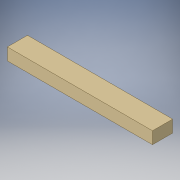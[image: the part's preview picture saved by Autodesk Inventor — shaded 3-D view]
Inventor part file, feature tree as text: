
AUTODESK INVENTOR PART (.ipt)
format: ipt  version: 2016 (Build 200138000, 138)  size: 89,088 bytes
history: native  units: in
note: dims shown in document units (in); Inventor stores cm internally (conversion verified against a paired STEP export)
features: extrude x1, sketch x1
ambient origin geometry x8: Origin, YZ Plane, XZ Plane, XY Plane, X Axis, Y Axis, Z Axis, Center Point
bodies: Solid1 (feature_tree)
feature tree (2):
  extrude  "Extrusion1"  Depth=2.5in
  sketch  "Sketch1"  dims[d0=1.5in d1=2.5in d2=18.0in d3=0.0in]
